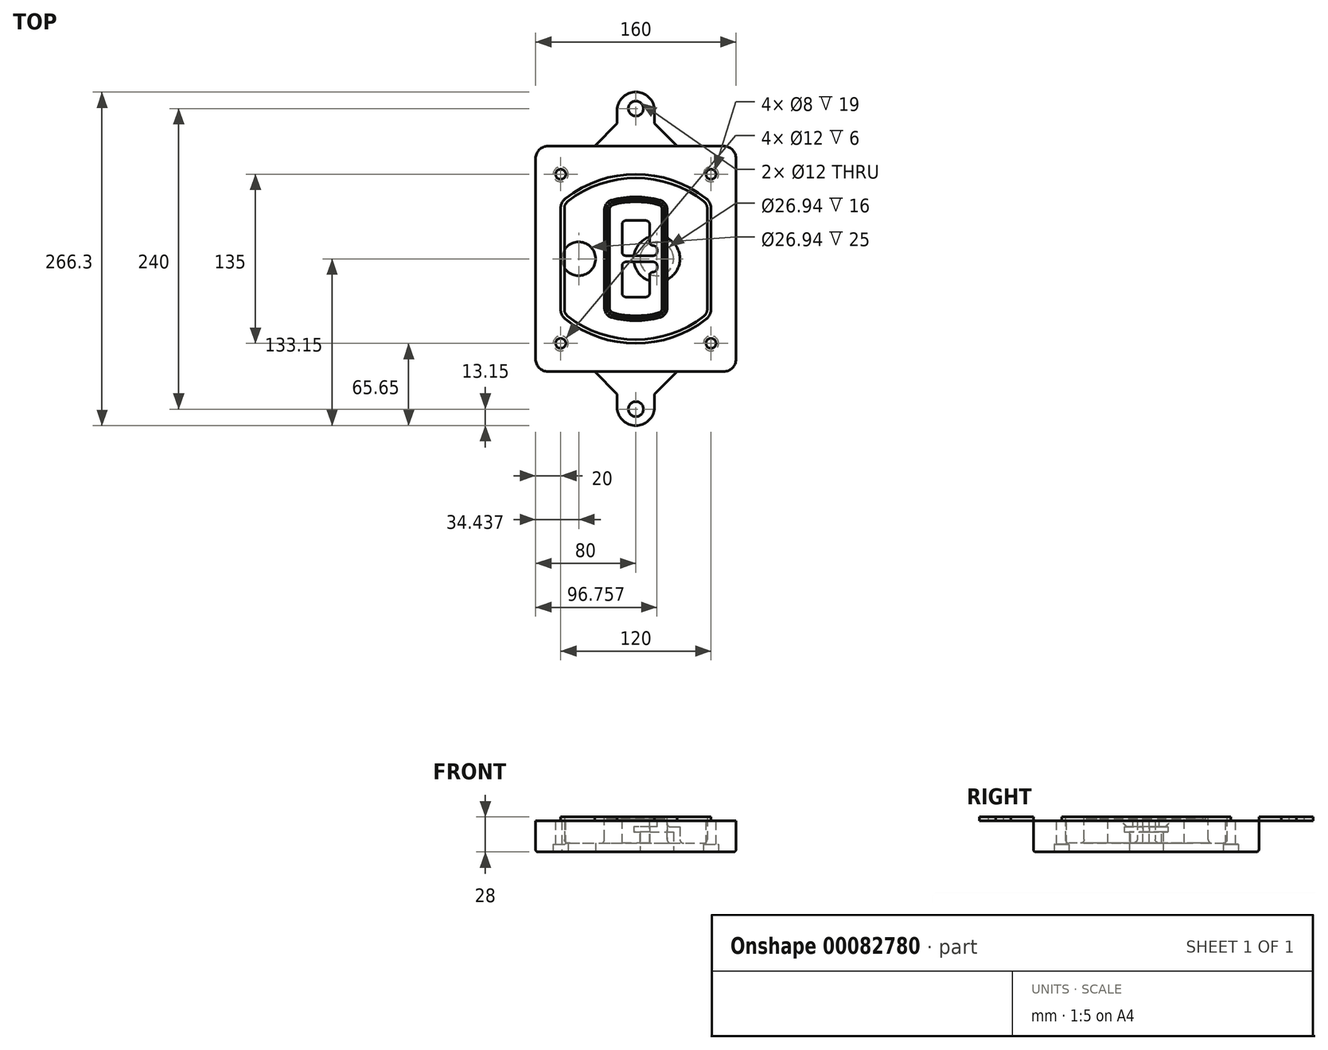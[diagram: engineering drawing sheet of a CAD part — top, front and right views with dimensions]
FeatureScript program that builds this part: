
annotation { "Feature Type Name" : "Feature", "Feature Type Description" : "" }
export const myFeature = defineFeature(function(context is Context, id is Id, definition is map)
    precondition{}
    {
        {
            var Q0;
            Q0=qCreatedBy(makeId("Top.planeOp"),FACE);
            var sketch = newSketch(context, id + "F0", { "sketchPlane" : qUnion([Q0])});
            skPoint(sketch, "E0.rect.middle", {"position": v(0, 0) * mm});
            skLineSegment(sketch, "E1.bottom", {"start": v(-70, -90) * mm, "end": v(70, -90) * mm});
            skLineSegment(sketch, "E1.top", {"start": v(-70, 90) * mm, "end": v(70, 90) * mm});
            skLineSegment(sketch, "E1.left", {"start": v(-80, -80) * mm, "end": v(-80, 80) * mm});
            skLineSegment(sketch, "E1.right", {"start": v(80, -80) * mm, "end": v(80, 80) * mm});
            skLineSegment(sketch, "E2", {"start": v(-80, 90) * mm, "end": v(80, -90) * mm, "construction": true});
            skLineSegment(sketch, "E3", {"start": v(80, 90) * mm, "end": v(-80, -90) * mm, "construction": true});
            skCircle(sketch, "E4", {"center": v(-60, 67.5) * mm, "radius": 4 * mm});
            skCircle(sketch, "E5", {"center": v(60, 67.5) * mm, "radius": 4 * mm});
            skCircle(sketch, "E6", {"center": v(60, -67.5) * mm, "radius": 4 * mm});
            skCircle(sketch, "E7", {"center": v(-60, -67.5) * mm, "radius": 4 * mm});
            skLineSegment(sketch, "E8", {"start": v(-60, 67.5) * mm, "end": v(60, 67.5) * mm, "construction": true});
            skLineSegment(sketch, "E9", {"start": v(60, 67.5) * mm, "end": v(60, -67.5) * mm, "construction": true});
            skLineSegment(sketch, "E10", {"start": v(60, -67.5) * mm, "end": v(-60, -67.5) * mm, "construction": true});
            skLineSegment(sketch, "E11", {"start": v(-60, -67.5) * mm, "end": v(-60, 67.5) * mm, "construction": true});
            skLineSegment(sketch, "E12", {"start": v(-60, 40.3) * mm, "end": v(-60, -40.3) * mm});
            skLineSegment(sketch, "E13", {"start": v(60, 40.3) * mm, "end": v(60, -40.3) * mm});
            skArc(sketch, "E14", {"start": v(56.15, 48.18) * mm, "mid": v(0, 67.5) * mm, "end": v(-56.15, 48.18) * mm});
            skArc(sketch, "E15", {"start": v(-56.15, -48.18) * mm, "mid": v(0, -67.5) * mm, "end": v(56.15, -48.18) * mm});
            skLineSegment(sketch, "E16", {"start": v(-60, 0) * mm, "end": v(60, 0) * mm, "construction": true});
            skPoint(sketch, "E17.visualSharp", {"position": v(-60, -45) * mm});
            skArc(sketch, "E17.filletArc", {"start": v(-60, -40.3) * mm, "mid": v(-58.99, -44.68) * mm, "end": v(-56.15, -48.18) * mm});
            skPoint(sketch, "E18.visualSharp", {"position": v(-60, 45) * mm});
            skArc(sketch, "E18.filletArc", {"start": v(-56.15, 48.18) * mm, "mid": v(-58.99, 44.68) * mm, "end": v(-60, 40.3) * mm});
            skPoint(sketch, "E19.visualSharp", {"position": v(60, 45) * mm});
            skArc(sketch, "E19.filletArc", {"start": v(60, 40.3) * mm, "mid": v(58.99, 44.68) * mm, "end": v(56.15, 48.18) * mm});
            skPoint(sketch, "E20.visualSharp", {"position": v(60, -45) * mm});
            skArc(sketch, "E20.filletArc", {"start": v(56.15, -48.18) * mm, "mid": v(58.99, -44.68) * mm, "end": v(60, -40.3) * mm});
            skPoint(sketch, "E21.visualSharp", {"position": v(-80, 90) * mm});
            skArc(sketch, "E21.filletArc", {"start": v(-70, 90) * mm, "mid": v(-77.07, 87.07) * mm, "end": v(-80, 80) * mm});
            skPoint(sketch, "E22.visualSharp", {"position": v(80, 90) * mm});
            skArc(sketch, "E22.filletArc", {"start": v(80, 80) * mm, "mid": v(77.07, 87.07) * mm, "end": v(70, 90) * mm});
            skPoint(sketch, "E23.visualSharp", {"position": v(80, -90) * mm});
            skArc(sketch, "E23.filletArc", {"start": v(70, -90) * mm, "mid": v(77.07, -87.07) * mm, "end": v(80, -80) * mm});
            skPoint(sketch, "E24.visualSharp", {"position": v(-80, -90) * mm});
            skArc(sketch, "E24.filletArc", {"start": v(-80, -80) * mm, "mid": v(-77.07, -87.07) * mm, "end": v(-70, -90) * mm});
            skArc(sketch, "E25.0", {"start": v(57, 40.3) * mm, "mid": v(56.3, 43.36) * mm, "end": v(54.3, 45.81) * mm});
            skLineSegment(sketch, "E25.1", {"start": v(57, 40.3) * mm, "end": v(57, -40.3) * mm});
            skArc(sketch, "E25.2", {"start": v(54.3, -45.81) * mm, "mid": v(56.3, -43.36) * mm, "end": v(57, -40.3) * mm});
            skArc(sketch, "E25.3", {"start": v(-54.3, -45.81) * mm, "mid": v(0, -64.5) * mm, "end": v(54.3, -45.81) * mm});
            skArc(sketch, "E25.4", {"start": v(-57, -40.3) * mm, "mid": v(-56.3, -43.36) * mm, "end": v(-54.3, -45.81) * mm});
            skArc(sketch, "E25.5", {"start": v(54.3, 45.81) * mm, "mid": v(0, 64.5) * mm, "end": v(-54.3, 45.81) * mm});
            skLineSegment(sketch, "E25.6", {"start": v(-57, 40.3) * mm, "end": v(-57, -40.3) * mm});
            skArc(sketch, "E25.7", {"start": v(-54.3, 45.81) * mm, "mid": v(-56.3, 43.36) * mm, "end": v(-57, 40.3) * mm});
            skArc(sketch, "E26.0", {"start": v(-58.62, 51.33) * mm, "mid": v(-62.58, 46.43) * mm, "end": v(-64, 40.3) * mm});
            skArc(sketch, "E26.1", {"start": v(58.62, 51.33) * mm, "mid": v(0, 71.5) * mm, "end": v(-58.62, 51.33) * mm});
            skArc(sketch, "E26.2", {"start": v(64, 40.3) * mm, "mid": v(62.58, 46.43) * mm, "end": v(58.62, 51.33) * mm});
            skLineSegment(sketch, "E26.3", {"start": v(64, 40.3) * mm, "end": v(64, -40.3) * mm});
            skArc(sketch, "E26.4", {"start": v(58.62, -51.33) * mm, "mid": v(62.58, -46.43) * mm, "end": v(64, -40.3) * mm});
            skLineSegment(sketch, "E26.5", {"start": v(-64, 40.3) * mm, "end": v(-64, -40.3) * mm});
            skArc(sketch, "E26.6", {"start": v(-58.62, -51.33) * mm, "mid": v(0, -71.5) * mm, "end": v(58.62, -51.33) * mm});
            skArc(sketch, "E26.7", {"start": v(-64, -40.3) * mm, "mid": v(-62.58, -46.43) * mm, "end": v(-58.62, -51.33) * mm});
            skSolve(sketch);
        }
        {
            var Q0;
            Q0=makeQuery(id+"F0.imprint","IMPRINT",FACE,{"disambiguationData":[TD([[makeQuery(id+"F0.imprint","IMPRINT",EDGE,{"derivedFrom":sQuery(id+"F0.wireOp",EDGE,"E1.bottom")}),1.0]])]});
            var Q1;
            Q1=makeQuery(id+"F0.imprint","IMPRINT",FACE,{"disambiguationData":[TD([[makeQuery(id+"F0.imprint","IMPRINT",EDGE,{"derivedFrom":sQuery(id+"F0.wireOp",EDGE,"E12")}),1.0]])]});
            var Q2;
            Q2=makeQuery(id+"F0.imprint","IMPRINT",FACE,{"disambiguationData":[TD([[makeQuery(id+"F0.imprint","IMPRINT",EDGE,{"derivedFrom":sQuery(id+"F0.wireOp",EDGE,"E25.0")}),1.0]])]});
            var Q3;
            Q3=makeQuery(id+"F0.imprint","IMPRINT",FACE,{"disambiguationData":[TD([[makeQuery(id+"F0.imprint","IMPRINT",EDGE,{"derivedFrom":sQuery(id+"F0.wireOp",EDGE,"E12")}),-1.0]])]});
            extrude(context, id + "F1", {"entities" : qUnion([Q0, Q1, Q2, Q3]), "oppositeDirection" : true, "depth" : 25 * mm});
        }
        {
            var Q0;
            Q0=makeQuery(id+"F0.imprint","IMPRINT",FACE,{"disambiguationData":[TD([[makeQuery(id+"F0.imprint","IMPRINT",EDGE,{"derivedFrom":sQuery(id+"F0.wireOp",EDGE,"E12")}),1.0]])]});
            extrude(context, id + "F2", {"entities" : qUnion([Q0]), "operationType" : NewBodyOperationType.ADD, "depth" : 3 * mm});
        }
        {
            var Q0;
            Q0=makeQuery(id+"F0.imprint","IMPRINT",FACE,{"disambiguationData":[TD([[makeQuery(id+"F0.imprint","IMPRINT",EDGE,{"derivedFrom":sQuery(id+"F0.wireOp",EDGE,"E25.0")}),1.0]])]});
            extrude(context, id + "F3", {"entities" : qUnion([Q0]), "operationType" : NewBodyOperationType.REMOVE, "oppositeDirection" : true, "depth" : 18 * mm});
        }
        {
            var Q0;
            Q0=makeQuery(id+"F2.opExtrude","CAP_FACE",FACE,{"disambiguationData":[OSD([sQuery(id+"F0.wireOp",EDGE,"E12"),sQuery(id+"F0.wireOp",EDGE,"E13"),sQuery(id+"F0.wireOp",EDGE,"E14"),sQuery(id+"F0.wireOp",EDGE,"E15"),sQuery(id+"F0.wireOp",EDGE,"E17.filletArc"),sQuery(id+"F0.wireOp",EDGE,"E18.filletArc"),sQuery(id+"F0.wireOp",EDGE,"E19.filletArc"),sQuery(id+"F0.wireOp",EDGE,"E20.filletArc"),sQuery(id+"F0.wireOp",EDGE,"E25.0"),sQuery(id+"F0.wireOp",EDGE,"E25.1"),sQuery(id+"F0.wireOp",EDGE,"E25.2"),sQuery(id+"F0.wireOp",EDGE,"E25.3"),sQuery(id+"F0.wireOp",EDGE,"E25.4"),sQuery(id+"F0.wireOp",EDGE,"E25.5"),sQuery(id+"F0.wireOp",EDGE,"E25.6"),sQuery(id+"F0.wireOp",EDGE,"E25.7")])],"isStart":false});
            var sketch = newSketch(context, id + "F4", { "sketchPlane" : qUnion([Q0])});
            skArc(sketch, "E27.0", {"start": v(-19.08, -46.97) * mm, "mid": v(0, -49.5) * mm, "end": v(19.08, -46.97) * mm});
            skArc(sketch, "E28.0", {"start": v(19.08, 46.97) * mm, "mid": v(0, 49.5) * mm, "end": v(-19.08, 46.97) * mm});
            skLineSegment(sketch, "E29", {"start": v(-25, 39.25) * mm, "end": v(-25, -39.25) * mm});
            skLineSegment(sketch, "E30", {"start": v(25, 39.25) * mm, "end": v(25, -39.25) * mm});
            skLineSegment(sketch, "E31", {"start": v(-25, 45.1) * mm, "end": v(25, 45.1) * mm, "construction": true});
            skLineSegment(sketch, "E32", {"start": v(-25, -45.1) * mm, "end": v(25, -45.1) * mm, "construction": true});
            skPoint(sketch, "E33.visualSharp", {"position": v(-25, 45.1) * mm});
            skArc(sketch, "E33.filletArc", {"start": v(-19.08, 46.97) * mm, "mid": v(-23.35, 44.11) * mm, "end": v(-25, 39.25) * mm});
            skPoint(sketch, "E34.visualSharp", {"position": v(25, 45.1) * mm});
            skArc(sketch, "E34.filletArc", {"start": v(25, 39.25) * mm, "mid": v(23.35, 44.11) * mm, "end": v(19.08, 46.97) * mm});
            skPoint(sketch, "E35.visualSharp", {"position": v(25, -45.1) * mm});
            skArc(sketch, "E35.filletArc", {"start": v(19.08, -46.97) * mm, "mid": v(23.35, -44.11) * mm, "end": v(25, -39.25) * mm});
            skPoint(sketch, "E36.visualSharp", {"position": v(-25, -45.1) * mm});
            skArc(sketch, "E36.filletArc", {"start": v(-25, -39.25) * mm, "mid": v(-23.35, -44.11) * mm, "end": v(-19.08, -46.97) * mm});
            skArc(sketch, "E37.0", {"start": v(54.3, 45.81) * mm, "mid": v(0, 64.5) * mm, "end": v(-54.3, 45.81) * mm});
            skArc(sketch, "E37.1", {"start": v(-54.3, 45.81) * mm, "mid": v(-56.3, 43.36) * mm, "end": v(-57, 40.3) * mm});
            skLineSegment(sketch, "E37.2", {"start": v(-57, 40.3) * mm, "end": v(-57, -40.3) * mm});
            skArc(sketch, "E37.3", {"start": v(-57, -40.3) * mm, "mid": v(-56.3, -43.36) * mm, "end": v(-54.3, -45.81) * mm});
            skArc(sketch, "E37.4", {"start": v(-54.3, -45.81) * mm, "mid": v(0, -64.5) * mm, "end": v(54.3, -45.81) * mm});
            skArc(sketch, "E37.5", {"start": v(54.3, -45.81) * mm, "mid": v(56.3, -43.36) * mm, "end": v(57, -40.3) * mm});
            skLineSegment(sketch, "E37.6", {"start": v(57, 40.3) * mm, "end": v(57, -40.3) * mm});
            skArc(sketch, "E37.7", {"start": v(57, 40.3) * mm, "mid": v(56.3, 43.36) * mm, "end": v(54.3, 45.81) * mm});
            skLineSegment(sketch, "E38.0", {"start": v(23, 39.25) * mm, "end": v(23, -39.25) * mm});
            skArc(sketch, "E38.1", {"start": v(18.56, -45.04) * mm, "mid": v(21.76, -42.9) * mm, "end": v(23, -39.25) * mm});
            skArc(sketch, "E38.2", {"start": v(-18.56, -45.04) * mm, "mid": v(0, -47.5) * mm, "end": v(18.56, -45.04) * mm});
            skArc(sketch, "E38.3", {"start": v(-23, -39.25) * mm, "mid": v(-21.76, -42.9) * mm, "end": v(-18.56, -45.04) * mm});
            skLineSegment(sketch, "E38.4", {"start": v(-23, 39.25) * mm, "end": v(-23, -39.25) * mm});
            skArc(sketch, "E38.5", {"start": v(23, 39.25) * mm, "mid": v(21.76, 42.9) * mm, "end": v(18.56, 45.04) * mm});
            skArc(sketch, "E38.6", {"start": v(-18.56, 45.04) * mm, "mid": v(-21.76, 42.9) * mm, "end": v(-23, 39.25) * mm});
            skArc(sketch, "E38.7", {"start": v(18.56, 45.04) * mm, "mid": v(0, 47.5) * mm, "end": v(-18.56, 45.04) * mm});
            skArc(sketch, "E39.0", {"start": v(21, 39.25) * mm, "mid": v(20.18, 41.68) * mm, "end": v(18.04, 43.1) * mm});
            skLineSegment(sketch, "E39.1", {"start": v(21, 39.25) * mm, "end": v(21, -39.25) * mm});
            skArc(sketch, "E39.2", {"start": v(18.04, -43.1) * mm, "mid": v(20.18, -41.68) * mm, "end": v(21, -39.25) * mm});
            skArc(sketch, "E39.3", {"start": v(-18.04, -43.1) * mm, "mid": v(0, -45.5) * mm, "end": v(18.04, -43.1) * mm});
            skArc(sketch, "E39.4", {"start": v(-21, -39.25) * mm, "mid": v(-20.18, -41.68) * mm, "end": v(-18.04, -43.1) * mm});
            skArc(sketch, "E39.5", {"start": v(18.04, 43.1) * mm, "mid": v(0, 45.5) * mm, "end": v(-18.04, 43.1) * mm});
            skLineSegment(sketch, "E39.6", {"start": v(-21, 39.25) * mm, "end": v(-21, -39.25) * mm});
            skArc(sketch, "E39.7", {"start": v(-18.04, 43.1) * mm, "mid": v(-20.18, 41.68) * mm, "end": v(-21, 39.25) * mm});
            skLineSegment(sketch, "E40", {"start": v(-25, 0) * mm, "end": v(25, 0) * mm, "construction": true});
            skLineSegment(sketch, "E41", {"start": v(-11, 5.5) * mm, "end": v(-11, 27.5) * mm});
            skLineSegment(sketch, "E42", {"start": v(-8, 30.5) * mm, "end": v(8, 30.5) * mm});
            skLineSegment(sketch, "E43", {"start": v(11, 27.5) * mm, "end": v(11, 13.5) * mm});
            skLineSegment(sketch, "E44", {"start": v(14, 10.5) * mm, "end": v(14, 10.5) * mm});
            skLineSegment(sketch, "E45", {"start": v(17, 7.5) * mm, "end": v(17, 5.5) * mm});
            skLineSegment(sketch, "E46", {"start": v(14, 2.5) * mm, "end": v(-8, 2.5) * mm});
            skPoint(sketch, "E47.visualSharp", {"position": v(-11, 30.5) * mm});
            skArc(sketch, "E47.filletArc", {"start": v(-8, 30.5) * mm, "mid": v(-10.12, 29.62) * mm, "end": v(-11, 27.5) * mm});
            skPoint(sketch, "E48.visualSharp", {"position": v(11, 30.5) * mm});
            skArc(sketch, "E48.filletArc", {"start": v(11, 27.5) * mm, "mid": v(10.12, 29.62) * mm, "end": v(8, 30.5) * mm});
            skPoint(sketch, "E49.visualSharp", {"position": v(11, 10.5) * mm});
            skArc(sketch, "E49.filletArc", {"start": v(11, 13.5) * mm, "mid": v(11.88, 11.38) * mm, "end": v(14, 10.5) * mm});
            skPoint(sketch, "E50.visualSharp", {"position": v(17, 10.5) * mm});
            skArc(sketch, "E50.filletArc", {"start": v(17, 7.5) * mm, "mid": v(16.12, 9.62) * mm, "end": v(14, 10.5) * mm});
            skPoint(sketch, "E51.visualSharp", {"position": v(17, 2.5) * mm});
            skArc(sketch, "E51.filletArc", {"start": v(14, 2.5) * mm, "mid": v(16.12, 3.38) * mm, "end": v(17, 5.5) * mm});
            skPoint(sketch, "E52.visualSharp", {"position": v(-11, 2.5) * mm});
            skArc(sketch, "E52.filletArc", {"start": v(-11, 5.5) * mm, "mid": v(-10.12, 3.38) * mm, "end": v(-8, 2.5) * mm});
            skLineSegment(sketch, "E53.0.MirrorCS", {"start": v(14, -2.5) * mm, "end": v(-8, -2.5) * mm});
            skArc(sketch, "E54.0.MirrorCS", {"start": v(-11, -5.5) * mm, "mid": v(-10.12, -3.38) * mm, "end": v(-8, -2.5) * mm});
            skLineSegment(sketch, "E55.0.MirrorCS", {"start": v(-11, -5.5) * mm, "end": v(-11, -27.5) * mm});
            skArc(sketch, "E56.0.MirrorCS", {"start": v(-8, -30.5) * mm, "mid": v(-10.12, -29.62) * mm, "end": v(-11, -27.5) * mm});
            skLineSegment(sketch, "E57.0.MirrorCS", {"start": v(-8, -30.5) * mm, "end": v(8, -30.5) * mm});
            skArc(sketch, "E58.0.MirrorCS", {"start": v(11, -27.5) * mm, "mid": v(10.12, -29.62) * mm, "end": v(8, -30.5) * mm});
            skLineSegment(sketch, "E59.0.MirrorCS", {"start": v(11, -27.5) * mm, "end": v(11, -13.5) * mm});
            skArc(sketch, "E60.0.MirrorCS", {"start": v(11, -13.5) * mm, "mid": v(11.88, -11.38) * mm, "end": v(14, -10.5) * mm});
            skArc(sketch, "E61.0.MirrorCS", {"start": v(17, -7.5) * mm, "mid": v(16.12, -9.62) * mm, "end": v(14, -10.5) * mm});
            skLineSegment(sketch, "E62.0.MirrorCS", {"start": v(17, -7.5) * mm, "end": v(17, -5.5) * mm});
            skArc(sketch, "E63.0.MirrorCS", {"start": v(14, -2.5) * mm, "mid": v(16.12, -3.38) * mm, "end": v(17, -5.5) * mm});
            skSolve(sketch);
        }
        {
            var Q0;
            Q0=makeQuery(id+"F4.imprint","IMPRINT",FACE,{"disambiguationData":[TD([[makeQuery(id+"F4.imprint","IMPRINT",EDGE,{"derivedFrom":sQuery(id+"F4.wireOp",EDGE,"E27.0")}),1.0]])]});
            var Q1;
            Q1=makeQuery(id+"F4.imprint","IMPRINT",FACE,{"disambiguationData":[TD([[makeQuery(id+"F4.imprint","IMPRINT",EDGE,{"derivedFrom":sQuery(id+"F4.wireOp",EDGE,"E38.0")}),-1.0]])]});
            var Q2;
            Q2=makeQuery(id+"F4.imprint","IMPRINT",FACE,{"disambiguationData":[TD([[makeQuery(id+"F4.imprint","IMPRINT",EDGE,{"derivedFrom":sQuery(id+"F4.wireOp",EDGE,"E39.0")}),1.0]])]});
            extrude(context, id + "F5", {"entities" : qUnion([Q0, Q1, Q2]), "operationType" : NewBodyOperationType.ADD, "endBound" : BoundingType.UP_TO_NEXT, "oppositeDirection" : true, "depth" : 25 * mm});
        }
        {
            var Q0;
            Q0=makeQuery(id+"F4.imprint","IMPRINT",FACE,{"disambiguationData":[TD([[makeQuery(id+"F4.imprint","IMPRINT",EDGE,{"derivedFrom":sQuery(id+"F4.wireOp",EDGE,"E38.0")}),-1.0]])]});
            extrude(context, id + "F6", {"entities" : qUnion([Q0]), "operationType" : NewBodyOperationType.REMOVE, "oppositeDirection" : true, "depth" : 2 * mm});
        }
        {
            var Q0;
            Q0=makeQuery(id+"F1.opExtrude","CAP_FACE",FACE,{"disambiguationData":[OSD([sQuery(id+"F0.wireOp",EDGE,"E1.bottom"),sQuery(id+"F0.wireOp",EDGE,"E1.top"),sQuery(id+"F0.wireOp",EDGE,"E1.left"),sQuery(id+"F0.wireOp",EDGE,"E1.right"),sQuery(id+"F0.wireOp",EDGE,"E4"),sQuery(id+"F0.wireOp",EDGE,"E5"),sQuery(id+"F0.wireOp",EDGE,"E6"),sQuery(id+"F0.wireOp",EDGE,"E7"),sQuery(id+"F0.wireOp",EDGE,"E21.filletArc"),sQuery(id+"F0.wireOp",EDGE,"E22.filletArc"),sQuery(id+"F0.wireOp",EDGE,"E23.filletArc"),sQuery(id+"F0.wireOp",EDGE,"E24.filletArc")])],"isStart":false});
            var sketch = newSketch(context, id + "F7", { "sketchPlane" : qUnion([Q0])});
            skCircle(sketch, "E64", {"center": v(16.76, 0) * mm, "radius": 13.47 * mm});
            skCircle(sketch, "E65", {"center": v(-45.56, 0) * mm, "radius": 13.47 * mm});
            skLineSegment(sketch, "E66", {"start": v(80, 0) * mm, "end": v(-80, 0) * mm});
            skCircle(sketch, "E67", {"center": v(16.76, 0) * mm, "radius": 18.47 * mm});
            skCircle(sketch, "E68", {"center": v(60, -67.5) * mm, "radius": 6 * mm});
            skCircle(sketch, "E69", {"center": v(-60, -67.5) * mm, "radius": 6 * mm});
            skCircle(sketch, "E70", {"center": v(-60, 67.5) * mm, "radius": 6 * mm});
            skCircle(sketch, "E71", {"center": v(60, 67.5) * mm, "radius": 6 * mm});
            skSolve(sketch);
        }
        {
            var Q0;
            {var subQ1=sQuery(id+"F7.wireOp",EDGE,"E66");var subQ4=sQuery(id+"F7.wireOp",EDGE,"E64");var subQ6=makeQuery(id+"F7.imprint","INTERSECT",VERTEX,{"disambiguationData":[OD(0.0)],"derivedFrom":[subQ4,subQ1]});Q0=makeQuery(id+"F7.imprint","IMPRINT",FACE,{"disambiguationData":[TD([[makeQuery(id+"F7.imprint","IMPRINT",EDGE,{"disambiguationData":[TD([[subQ6,-1.0]])],"derivedFrom":subQ4}),-1.0]])]});}
            var Q1;
            {var subQ0=sQuery(id+"F7.wireOp",EDGE,"E66");var subQ1=sQuery(id+"F7.wireOp",EDGE,"E64");var subQ3=makeQuery(id+"F7.imprint","INTERSECT",VERTEX,{"disambiguationData":[OD(0.0)],"derivedFrom":[subQ1,subQ0]});Q1=makeQuery(id+"F7.imprint","IMPRINT",FACE,{"disambiguationData":[TD([[makeQuery(id+"F7.imprint","IMPRINT",EDGE,{"disambiguationData":[TD([[subQ3,-1.0]])],"derivedFrom":subQ1}),1.0]])]});}
            var Q2;
            {var subQ0=sQuery(id+"F7.wireOp",EDGE,"E66");var subQ1=sQuery(id+"F7.wireOp",EDGE,"E64");var subQ3=makeQuery(id+"F7.imprint","INTERSECT",VERTEX,{"disambiguationData":[OD(0.0)],"derivedFrom":[subQ1,subQ0]});Q2=makeQuery(id+"F7.imprint","IMPRINT",FACE,{"disambiguationData":[TD([[makeQuery(id+"F7.imprint","IMPRINT",EDGE,{"disambiguationData":[TD([[subQ3,1.0]])],"derivedFrom":subQ1}),1.0]])]});}
            var Q3;
            {var subQ1=sQuery(id+"F7.wireOp",EDGE,"E66");var subQ4=sQuery(id+"F7.wireOp",EDGE,"E64");var subQ6=makeQuery(id+"F7.imprint","INTERSECT",VERTEX,{"disambiguationData":[OD(0.0)],"derivedFrom":[subQ4,subQ1]});Q3=makeQuery(id+"F7.imprint","IMPRINT",FACE,{"disambiguationData":[TD([[makeQuery(id+"F7.imprint","IMPRINT",EDGE,{"disambiguationData":[TD([[subQ6,1.0]])],"derivedFrom":subQ4}),-1.0]])]});}
            extrude(context, id + "F8", {"entities" : qUnion([Q0, Q1, Q2, Q3]), "operationType" : NewBodyOperationType.ADD, "oppositeDirection" : true, "depth" : 20 * mm});
        }
        {
            var Q0;
            {var subQ0=sQuery(id+"F7.wireOp",EDGE,"E66");var subQ1=sQuery(id+"F7.wireOp",EDGE,"E64");var subQ3=makeQuery(id+"F7.imprint","INTERSECT",VERTEX,{"disambiguationData":[OD(0.0)],"derivedFrom":[subQ1,subQ0]});Q0=makeQuery(id+"F7.imprint","IMPRINT",FACE,{"disambiguationData":[TD([[makeQuery(id+"F7.imprint","IMPRINT",EDGE,{"disambiguationData":[TD([[subQ3,-1.0]])],"derivedFrom":subQ1}),1.0]])]});}
            var Q1;
            {var subQ0=sQuery(id+"F7.wireOp",EDGE,"E66");var subQ1=sQuery(id+"F7.wireOp",EDGE,"E64");var subQ3=makeQuery(id+"F7.imprint","INTERSECT",VERTEX,{"disambiguationData":[OD(0.0)],"derivedFrom":[subQ1,subQ0]});Q1=makeQuery(id+"F7.imprint","IMPRINT",FACE,{"disambiguationData":[TD([[makeQuery(id+"F7.imprint","IMPRINT",EDGE,{"disambiguationData":[TD([[subQ3,1.0]])],"derivedFrom":subQ1}),1.0]])]});}
            extrude(context, id + "F9", {"entities" : qUnion([Q0, Q1]), "operationType" : NewBodyOperationType.REMOVE, "oppositeDirection" : true, "depth" : 16 * mm});
        }
        {
            var Q0;
            {var subQ0=sQuery(id+"F7.wireOp",EDGE,"E66");var subQ1=sQuery(id+"F7.wireOp",EDGE,"E65");var subQ3=makeQuery(id+"F7.imprint","INTERSECT",VERTEX,{"disambiguationData":[OD(0.0)],"derivedFrom":[subQ1,subQ0]});Q0=makeQuery(id+"F7.imprint","IMPRINT",FACE,{"disambiguationData":[TD([[makeQuery(id+"F7.imprint","IMPRINT",EDGE,{"disambiguationData":[TD([[subQ3,-1.0]])],"derivedFrom":subQ1}),1.0]])]});}
            var Q1;
            {var subQ0=sQuery(id+"F7.wireOp",EDGE,"E66");var subQ1=sQuery(id+"F7.wireOp",EDGE,"E65");var subQ3=makeQuery(id+"F7.imprint","INTERSECT",VERTEX,{"disambiguationData":[OD(0.0)],"derivedFrom":[subQ1,subQ0]});Q1=makeQuery(id+"F7.imprint","IMPRINT",FACE,{"disambiguationData":[TD([[makeQuery(id+"F7.imprint","IMPRINT",EDGE,{"disambiguationData":[TD([[subQ3,1.0]])],"derivedFrom":subQ1}),1.0]])]});}
            extrude(context, id + "F10", {"entities" : qUnion([Q0, Q1]), "operationType" : NewBodyOperationType.REMOVE, "oppositeDirection" : true, "depth" : 25 * mm});
        }
        {
            var Q0;
            Q0=makeQuery(id+"F7.imprint","IMPRINT",FACE,{"disambiguationData":[TD([[makeQuery(id+"F7.imprint","IMPRINT",EDGE,{"derivedFrom":sQuery(id+"F7.wireOp",EDGE,"E68")}),1.0]])]});
            var Q1;
            Q1=makeQuery(id+"F7.imprint","IMPRINT",FACE,{"disambiguationData":[TD([[makeQuery(id+"F7.imprint","IMPRINT",EDGE,{"derivedFrom":makeQuery(id+"F1.opExtrude","CAP_EDGE",EDGE,{"disambiguationData":[OSD([sQuery(id+"F0.wireOp",EDGE,"E5")])],"isStart":false})}),-1.0]])]});
            var Q2;
            Q2=makeQuery(id+"F7.imprint","IMPRINT",FACE,{"disambiguationData":[TD([[makeQuery(id+"F7.imprint","IMPRINT",EDGE,{"derivedFrom":sQuery(id+"F7.wireOp",EDGE,"E69")}),1.0]])]});
            var Q3;
            Q3=makeQuery(id+"F7.imprint","IMPRINT",FACE,{"disambiguationData":[TD([[makeQuery(id+"F7.imprint","IMPRINT",EDGE,{"derivedFrom":makeQuery(id+"F1.opExtrude","CAP_EDGE",EDGE,{"disambiguationData":[OSD([sQuery(id+"F0.wireOp",EDGE,"E4")])],"isStart":false})}),-1.0]])]});
            var Q4;
            Q4=makeQuery(id+"F7.imprint","IMPRINT",FACE,{"disambiguationData":[TD([[makeQuery(id+"F7.imprint","IMPRINT",EDGE,{"derivedFrom":sQuery(id+"F7.wireOp",EDGE,"E70")}),1.0]])]});
            var Q5;
            Q5=makeQuery(id+"F7.imprint","IMPRINT",FACE,{"disambiguationData":[TD([[makeQuery(id+"F7.imprint","IMPRINT",EDGE,{"derivedFrom":makeQuery(id+"F1.opExtrude","CAP_EDGE",EDGE,{"disambiguationData":[OSD([sQuery(id+"F0.wireOp",EDGE,"E7")])],"isStart":false})}),-1.0]])]});
            var Q6;
            Q6=makeQuery(id+"F7.imprint","IMPRINT",FACE,{"disambiguationData":[TD([[makeQuery(id+"F7.imprint","IMPRINT",EDGE,{"derivedFrom":sQuery(id+"F7.wireOp",EDGE,"E71")}),1.0]])]});
            var Q7;
            Q7=makeQuery(id+"F7.imprint","IMPRINT",FACE,{"disambiguationData":[TD([[makeQuery(id+"F7.imprint","IMPRINT",EDGE,{"derivedFrom":makeQuery(id+"F1.opExtrude","CAP_EDGE",EDGE,{"disambiguationData":[OSD([sQuery(id+"F0.wireOp",EDGE,"E6")])],"isStart":false})}),-1.0]])]});
            extrude(context, id + "F11", {"entities" : qUnion([Q0, Q1, Q2, Q3, Q4, Q5, Q6, Q7]), "operationType" : NewBodyOperationType.REMOVE, "oppositeDirection" : true, "depth" : 6 * mm});
        }
        {
            var Q0;
            Q0=makeQuery(id+"F9.boolean.opBoolean","COPY",FACE,{"derivedFrom":makeQuery(id+"F9.opExtrude","CAP_FACE",FACE,{"disambiguationData":[OSD([sQuery(id+"F7.wireOp",EDGE,"E64")])],"isStart":false})});
            var sketch = newSketch(context, id + "F12", { "sketchPlane" : qUnion([Q0])});
            skArc(sketch, "E72.0", {"start": v(11, 17.55) * mm, "mid": v(2.57, 11.82) * mm, "end": v(-1.54, 2.5) * mm});
            skArc(sketch, "E72.1", {"start": v(-1.54, -2.5) * mm, "mid": v(2.57, -11.82) * mm, "end": v(11, -17.55) * mm});
            skLineSegment(sketch, "E73", {"start": v(-1.54, -2.5) * mm, "end": v(14, -2.5) * mm});
            skLineSegment(sketch, "E74.0", {"start": v(14, 2.5) * mm, "end": v(-1.54, 2.5) * mm});
            skArc(sketch, "E74.1", {"start": v(14, 2.5) * mm, "mid": v(16.12, 3.38) * mm, "end": v(17, 5.5) * mm});
            skLineSegment(sketch, "E74.2", {"start": v(17, 7.5) * mm, "end": v(17, 5.5) * mm});
            skArc(sketch, "E74.3", {"start": v(17, 7.5) * mm, "mid": v(16.12, 9.62) * mm, "end": v(14, 10.5) * mm});
            skArc(sketch, "E74.4", {"start": v(11, 13.5) * mm, "mid": v(11.88, 11.38) * mm, "end": v(14, 10.5) * mm});
            skLineSegment(sketch, "E74.5", {"start": v(11, 17.55) * mm, "end": v(11, 13.5) * mm});
            skLineSegment(sketch, "E74.7", {"start": v(14, -2.5) * mm, "end": v(-1.54, -2.5) * mm});
            skArc(sketch, "E74.8", {"start": v(14, -2.5) * mm, "mid": v(16.12, -3.38) * mm, "end": v(17, -5.5) * mm});
            skLineSegment(sketch, "E74.9", {"start": v(17, -7.5) * mm, "end": v(17, -5.5) * mm});
            skArc(sketch, "E74.10", {"start": v(17, -7.5) * mm, "mid": v(16.12, -9.62) * mm, "end": v(14, -10.5) * mm});
            skArc(sketch, "E74.11", {"start": v(11, -13.5) * mm, "mid": v(11.88, -11.38) * mm, "end": v(14, -10.5) * mm});
            skLineSegment(sketch, "E74.12", {"start": v(11, -17.55) * mm, "end": v(11, -13.5) * mm});
            skPoint(sketch, "E75.orphan", {"position": v(11, -27.5) * mm});
            skPoint(sketch, "E76.orphan", {"position": v(-8, -2.5) * mm});
            skPoint(sketch, "E77.orphan", {"position": v(-8, 2.5) * mm});
            skPoint(sketch, "E78.orphan", {"position": v(11, 27.5) * mm});
            skSolve(sketch);
        }
        {
            var Q0;
            {var subQ7=sQuery(id+"F12.wireOp",EDGE,"E72.0");var subQ14=sQuery(id+"F12.wireOp",EDGE,"E72.1");var subQ16=sQuery(id+"F12.wireOp",EDGE,"E74.1");var subQ18=sQuery(id+"F12.wireOp",EDGE,"E74.8");Q0=qUnion([makeQuery(id+"F12.imprint","IMPRINT",FACE,{"disambiguationData":[TD([[makeQuery(id+"F12.imprint","IMPRINT",EDGE,{"derivedFrom":subQ7}),1.0]])]}),makeQuery(id+"F12.imprint","IMPRINT",FACE,{"disambiguationData":[TD([[makeQuery(id+"F12.imprint","IMPRINT",EDGE,{"derivedFrom":subQ14}),1.0]])]}),makeQuery(id+"F12.imprint","IMPRINT",FACE,{"disambiguationData":[TD([[makeQuery(id+"F12.imprint","IMPRINT",EDGE,{"derivedFrom":subQ16}),1.0]])]}),makeQuery(id+"F12.imprint","IMPRINT",FACE,{"disambiguationData":[TD([[makeQuery(id+"F12.imprint","IMPRINT",EDGE,{"derivedFrom":subQ18}),-1.0]])]})]);}
            var Q1;
            Q1=makeQuery(id+"F5.boolean.opBoolean","SPLIT",FACE,{"disambiguationData":[TD([makeQuery(id+"F5.opExtrude","SWEPT_FACE",FACE,{"disambiguationData":[OSD([sQuery(id+"F4.wireOp",EDGE,"E41")])]})])],"derivedFrom":makeQuery(id+"F3.boolean.opBoolean","COPY",FACE,{"derivedFrom":makeQuery(id+"F3.opExtrude","CAP_FACE",FACE,{"disambiguationData":[OSD([sQuery(id+"F0.wireOp",EDGE,"E25.0"),sQuery(id+"F0.wireOp",EDGE,"E25.1"),sQuery(id+"F0.wireOp",EDGE,"E25.2"),sQuery(id+"F0.wireOp",EDGE,"E25.3"),sQuery(id+"F0.wireOp",EDGE,"E25.4"),sQuery(id+"F0.wireOp",EDGE,"E25.5"),sQuery(id+"F0.wireOp",EDGE,"E25.6"),sQuery(id+"F0.wireOp",EDGE,"E25.7")])],"isStart":false})})});
            extrude(context, id + "F13", {"entities" : qUnion([Q0]), "operationType" : NewBodyOperationType.REMOVE, "endBound" : BoundingType.UP_TO_SURFACE, "endBoundEntityFace" : qUnion([Q1]), "depth" : 25 * mm});
        }
        {
            var Q0;
            Q0=makeQuery(id+"F3.boolean.opBoolean","COPY",EDGE,{"derivedFrom":makeQuery(id+"F3.opExtrude","CAP_EDGE",EDGE,{"disambiguationData":[OSD([sQuery(id+"F0.wireOp",EDGE,"E25.6")])],"isStart":false})});
            var Q1;
            Q1=makeQuery(id+"F8.boolean.opBoolean","INTERSECT",EDGE,{"derivedFrom":[makeQuery(id+"F5.opExtrude","SWEPT_FACE",FACE,{"disambiguationData":[OSD([sQuery(id+"F4.wireOp",EDGE,"E30")])]}),makeQuery(id+"F8.opExtrude","CAP_FACE",FACE,{"disambiguationData":[OSD([sQuery(id+"F7.wireOp",EDGE,"E67")])],"isStart":false})]});
            var Q2;
            Q2=makeQuery(id+"F8.boolean.opBoolean","INTERSECT",EDGE,{"disambiguationData":[OD(1.0)],"derivedFrom":[makeQuery(id+"F5.opExtrude","SWEPT_FACE",FACE,{"disambiguationData":[OSD([sQuery(id+"F4.wireOp",EDGE,"E30")])]}),makeQuery(id+"F8.opExtrude","SWEPT_FACE",FACE,{"disambiguationData":[OSD([sQuery(id+"F7.wireOp",EDGE,"E67")])]})]});
            var Q3;
            {var subQ0=sQuery(id+"F4.wireOp",EDGE,"E30");Q3=makeQuery(id+"F8.boolean.opBoolean","SPLIT",EDGE,{"disambiguationData":[TD([makeQuery(id+"F5.opExtrude","SWEPT_FACE",FACE,{"disambiguationData":[OSD([sQuery(id+"F4.wireOp",EDGE,"E35.filletArc")])]})])],"derivedFrom":makeQuery(id+"F5.opExtrude","CAP_EDGE",EDGE,{"disambiguationData":[OSD([subQ0])],"isStart":false})});}
            var Q4;
            {var subQ0=sQuery(id+"F0.wireOp",EDGE,"E25.7");var subQ1=sQuery(id+"F0.wireOp",EDGE,"E25.1");var subQ2=sQuery(id+"F0.wireOp",EDGE,"E25.6");var subQ3=sQuery(id+"F0.wireOp",EDGE,"E25.5");var subQ4=sQuery(id+"F0.wireOp",EDGE,"E25.4");var subQ5=sQuery(id+"F0.wireOp",EDGE,"E25.0");var subQ6=sQuery(id+"F0.wireOp",EDGE,"E25.2");var subQ7=sQuery(id+"F0.wireOp",EDGE,"E25.3");Q4=makeQuery(id+"F8.boolean.opBoolean","INTERSECT",EDGE,{"derivedFrom":[makeQuery(id+"F5.boolean.opBoolean","SPLIT",FACE,{"disambiguationData":[TD([makeQuery(id+"F2.opExtrude","SWEPT_FACE",FACE,{"disambiguationData":[OSD([subQ5])]})])],"derivedFrom":makeQuery(id+"F3.boolean.opBoolean","COPY",FACE,{"derivedFrom":makeQuery(id+"F3.opExtrude","CAP_FACE",FACE,{"disambiguationData":[OSD([subQ5,subQ1,subQ6,subQ7,subQ4,subQ3,subQ2,subQ0])],"isStart":false})})}),makeQuery(id+"F8.opExtrude","SWEPT_FACE",FACE,{"disambiguationData":[OSD([sQuery(id+"F7.wireOp",EDGE,"E67")])]})]});}
            var Q5;
            Q5=makeQuery(id+"F8.boolean.opBoolean","INTERSECT",EDGE,{"disambiguationData":[OD(0.0)],"derivedFrom":[makeQuery(id+"F5.opExtrude","SWEPT_FACE",FACE,{"disambiguationData":[OSD([sQuery(id+"F4.wireOp",EDGE,"E30")])]}),makeQuery(id+"F8.opExtrude","SWEPT_FACE",FACE,{"disambiguationData":[OSD([sQuery(id+"F7.wireOp",EDGE,"E67")])]})]});
            fillet(context, id + "F14", {"entities" : qUnion([Q0, Q1, Q2, Q3, Q4, Q5]), "radius" : 3 * mm, "tangentPropagation" : true, "allowEdgeOverflow" : false});
        }
        {
            var Q0;
            Q0=makeQuery(id+"F1.opExtrude","CAP_EDGE",EDGE,{"disambiguationData":[OSD([sQuery(id+"F0.wireOp",EDGE,"E1.bottom")])],"isStart":false});
            fillet(context, id + "F15", {"entities" : qUnion([Q0]), "radius" : 2 * mm, "tangentPropagation" : true, "allowEdgeOverflow" : false});
        }
        {
            var Q0;
            {var subQ0=sQuery(id+"F0.wireOp",EDGE,"E22.filletArc");var subQ1=sQuery(id+"F0.wireOp",EDGE,"E7");var subQ2=sQuery(id+"F0.wireOp",EDGE,"E6");var subQ3=sQuery(id+"F0.wireOp",EDGE,"E5");var subQ4=sQuery(id+"F0.wireOp",EDGE,"E4");var subQ5=sQuery(id+"F0.wireOp",EDGE,"E1.bottom");var subQ6=sQuery(id+"F0.wireOp",EDGE,"E21.filletArc");var subQ7=sQuery(id+"F0.wireOp",EDGE,"E1.top");var subQ8=sQuery(id+"F0.wireOp",EDGE,"E1.left");var subQ9=sQuery(id+"F0.wireOp",EDGE,"E1.right");var subQ10=sQuery(id+"F0.wireOp",EDGE,"E23.filletArc");var subQ11=sQuery(id+"F0.wireOp",EDGE,"E24.filletArc");Q0=makeQuery(id+"F2.boolean.opBoolean","SPLIT",FACE,{"disambiguationData":[TD([makeQuery(id+"F1.opExtrude","SWEPT_FACE",FACE,{"disambiguationData":[OSD([subQ5])]})])],"derivedFrom":makeQuery(id+"F1.opExtrude","CAP_FACE",FACE,{"disambiguationData":[OSD([subQ5,subQ7,subQ8,subQ9,subQ4,subQ3,subQ2,subQ1,subQ6,subQ0,subQ10,subQ11])],"isStart":true})});}
            var sketch = newSketch(context, id + "F16", { "sketchPlane" : qUnion([Q0])});
            skLineSegment(sketch, "E79", {"start": v(-80, 0) * mm, "end": v(80, 0) * mm, "construction": true});
            skLineSegment(sketch, "E80", {"start": v(0, 90) * mm, "end": v(0, 120) * mm, "construction": true});
            skLineSegment(sketch, "E81", {"start": v(-32.89, 90) * mm, "end": v(-14.89, 108) * mm});
            skLineSegment(sketch, "E82", {"start": v(-14.89, 108) * mm, "end": v(-14.89, 120) * mm});
            skLineSegment(sketch, "E83", {"start": v(32.89, 90) * mm, "end": v(14.89, 108) * mm});
            skLineSegment(sketch, "E84", {"start": v(14.89, 108) * mm, "end": v(14.89, 120) * mm});
            skCircle(sketch, "E85", {"center": v(0, 120) * mm, "radius": 6 * mm});
            skArc(sketch, "E86", {"start": v(14.89, 120) * mm, "mid": v(0, 133.15) * mm, "end": v(-14.89, 120) * mm});
            skLineSegment(sketch, "E87", {"start": v(-32.89, 90) * mm, "end": v(32.89, 90) * mm});
            skLineSegment(sketch, "E88", {"start": v(0, 90) * mm, "end": v(32.89, 90) * mm});
            skLineSegment(sketch, "E89", {"start": v(0, 90) * mm, "end": v(-32.89, 90) * mm});
            skLineSegment(sketch, "E90.MirrorCS", {"start": v(-32.89, -90) * mm, "end": v(32.89, -90) * mm});
            skLineSegment(sketch, "E91.MirrorCS", {"start": v(14.89, -108) * mm, "end": v(14.89, -120) * mm});
            skCircle(sketch, "E92.MirrorC", {"center": v(0, -120) * mm, "radius": 6 * mm});
            skLineSegment(sketch, "E93.MirrorCS", {"start": v(32.89, -90) * mm, "end": v(14.89, -108) * mm});
            skLineSegment(sketch, "E94.MirrorCS", {"start": v(-32.89, -90) * mm, "end": v(-14.89, -108) * mm});
            skLineSegment(sketch, "E95.MirrorCS", {"start": v(-14.89, -108) * mm, "end": v(-14.89, -120) * mm});
            skArc(sketch, "E96.MirrorCS", {"start": v(14.89, -120) * mm, "mid": v(0, -133.15) * mm, "end": v(-14.89, -120) * mm});
            skLineSegment(sketch, "E97.MirrorCS", {"start": v(0, -90) * mm, "end": v(32.89, -90) * mm});
            skLineSegment(sketch, "E98.MirrorCS", {"start": v(0, -90) * mm, "end": v(0, -120) * mm, "construction": true});
            skLineSegment(sketch, "E99.MirrorCS", {"start": v(0, -90) * mm, "end": v(-32.89, -90) * mm});
            skSolve(sketch);
        }
        {
            var Q0;
            {var subQ5=sQuery(id+"F16.wireOp",EDGE,"E88");Q0=makeQuery(id+"F16.imprint","IMPRINT",FACE,{"disambiguationData":[TD([[makeQuery(id+"F16.imprint","IMPRINT",EDGE,{"derivedFrom":subQ5}),-1.0]])]});}
            var Q1;
            Q1=makeQuery(id+"F16.imprint","IMPRINT",FACE,{"disambiguationData":[TD([[makeQuery(id+"F16.imprint","IMPRINT",EDGE,{"derivedFrom":sQuery(id+"F16.wireOp",EDGE,"E81")}),-1.0]])]});
            var Q2;
            Q2=makeQuery(id+"F16.imprint","IMPRINT",FACE,{"disambiguationData":[TD([[makeQuery(id+"F16.imprint","IMPRINT",EDGE,{"derivedFrom":sQuery(id+"F16.wireOp",EDGE,"E91.MirrorCS")}),-1.0]])]});
            var Q3;
            Q3=makeQuery(id+"F2.opExtrude","CAP_FACE",FACE,{"disambiguationData":[OSD([sQuery(id+"F0.wireOp",EDGE,"E12"),sQuery(id+"F0.wireOp",EDGE,"E13"),sQuery(id+"F0.wireOp",EDGE,"E14"),sQuery(id+"F0.wireOp",EDGE,"E15"),sQuery(id+"F0.wireOp",EDGE,"E17.filletArc"),sQuery(id+"F0.wireOp",EDGE,"E18.filletArc"),sQuery(id+"F0.wireOp",EDGE,"E19.filletArc"),sQuery(id+"F0.wireOp",EDGE,"E20.filletArc"),sQuery(id+"F0.wireOp",EDGE,"E25.0"),sQuery(id+"F0.wireOp",EDGE,"E25.1"),sQuery(id+"F0.wireOp",EDGE,"E25.2"),sQuery(id+"F0.wireOp",EDGE,"E25.3"),sQuery(id+"F0.wireOp",EDGE,"E25.4"),sQuery(id+"F0.wireOp",EDGE,"E25.5"),sQuery(id+"F0.wireOp",EDGE,"E25.6"),sQuery(id+"F0.wireOp",EDGE,"E25.7")])],"isStart":false});
            extrude(context, id + "F17", {"entities" : qUnion([Q0, Q1, Q2]), "operationType" : NewBodyOperationType.ADD, "endBound" : BoundingType.UP_TO_SURFACE, "endBoundEntityFace" : qUnion([Q3]), "depth" : 25 * mm});
        }
    });
